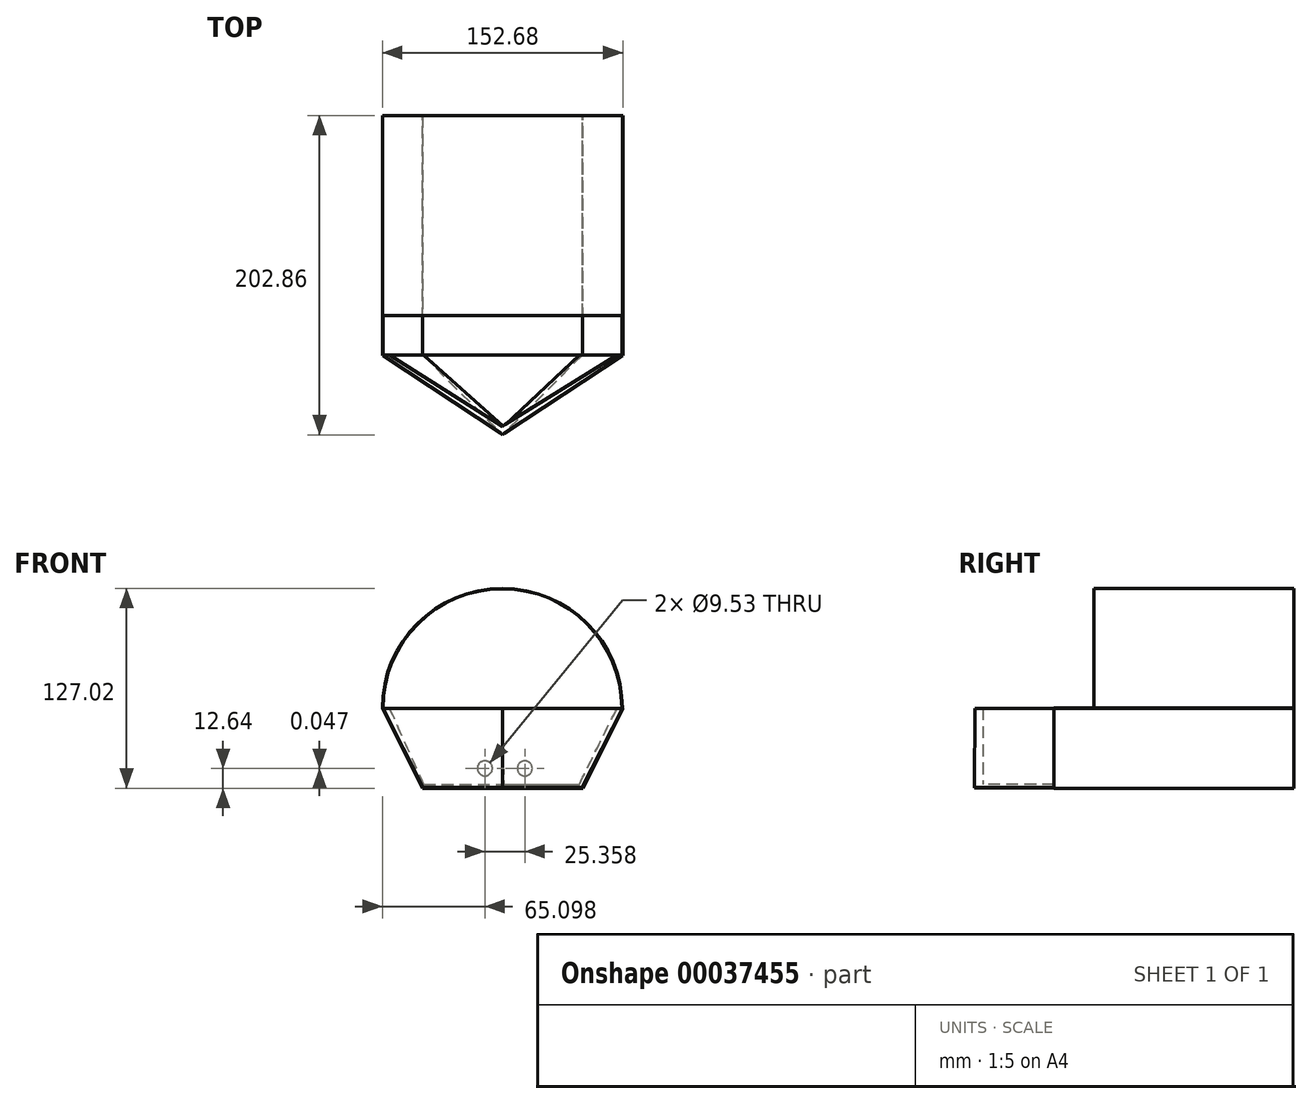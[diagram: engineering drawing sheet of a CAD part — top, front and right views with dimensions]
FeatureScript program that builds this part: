
annotation { "Feature Type Name" : "Feature", "Feature Type Description" : "" }
export const myFeature = defineFeature(function(context is Context, id is Id, definition is map)
    precondition{}
    {
        {
            var Q0;
            Q0=qCreatedBy(makeId("Top.planeOp"),FACE);
            var sketch = newSketch(context, id + "F0", { "sketchPlane" : qUnion([Q0])});
            skLineSegment(sketch, "E0.bottom", {"start": v(-53.58, 84.21) * mm, "end": v(98.82, 84.21) * mm});
            skLineSegment(sketch, "E0.top", {"start": v(-53.58, -68.19) * mm, "end": v(98.82, -68.19) * mm});
            skLineSegment(sketch, "E0.left", {"start": v(-53.58, 84.21) * mm, "end": v(-53.58, -68.19) * mm});
            skLineSegment(sketch, "E0.right", {"start": v(98.82, 84.21) * mm, "end": v(98.82, -68.19) * mm});
            skSolve(sketch);
        }
        {
            var Q0;
            Q0 = qSketchRegion(id + "F0", true);
            extrude(context, id + "F1", {"entities" : qUnion([Q0]), "depth" : 63.5 * mm});
        }
        {
            var Q0;
            Q0=makeQuery(id+"F1.opExtrude","CAP_FACE",FACE,{"disambiguationData":[OSD([sQuery(id+"F0.wireOp",EDGE,"E0.bottom"),sQuery(id+"F0.wireOp",EDGE,"E0.top"),sQuery(id+"F0.wireOp",EDGE,"E0.left"),sQuery(id+"F0.wireOp",EDGE,"E0.right")])],"isStart":false});
            var sketch = newSketch(context, id + "F2", { "sketchPlane" : qUnion([Q0])});
            skLineSegment(sketch, "E1.bottom", {"start": v(-53.26, 83.9) * mm, "end": v(98.5, 83.9) * mm});
            skLineSegment(sketch, "E1.top", {"start": v(-53.26, -67.87) * mm, "end": v(98.5, -67.87) * mm});
            skLineSegment(sketch, "E1.left", {"start": v(-53.26, 83.9) * mm, "end": v(-53.26, -67.87) * mm});
            skLineSegment(sketch, "E1.right", {"start": v(98.5, 83.9) * mm, "end": v(98.5, -67.87) * mm});
            skLineSegment(sketch, "E2", {"start": v(98.5, -5.97) * mm, "end": v(98.82, -5.97) * mm});
            skLineSegment(sketch, "E3", {"start": v(-53.26, -0.2) * mm, "end": v(-53.58, -0.2) * mm});
            skLineSegment(sketch, "E4", {"start": v(22.62, 83.9) * mm, "end": v(22.62, 84.21) * mm});
            skLineSegment(sketch, "E5", {"start": v(22.62, -67.87) * mm, "end": v(22.62, -68.19) * mm});
            skPoint(sketch, "E5.startSnap0", {"position": v(22.62, -68.19) * mm});
            skSolve(sketch);
        }
        {
            var Q0;
            Q0 = qSketchRegion(id + "F2", true);
            extrude(context, id + "F3", {"entities" : qUnion([Q0]), "operationType" : NewBodyOperationType.REMOVE, "oppositeDirection" : true, "depth" : 63.18 * mm});
        }
        {
            var Q0;
            Q0=makeQuery(id+"F1.opExtrude","CAP_FACE",FACE,{"disambiguationData":[OSD([sQuery(id+"F0.wireOp",EDGE,"E0.bottom"),sQuery(id+"F0.wireOp",EDGE,"E0.top"),sQuery(id+"F0.wireOp",EDGE,"E0.left"),sQuery(id+"F0.wireOp",EDGE,"E0.right")])],"isStart":false});
            extrude(context, id + "F4", {"entities" : qUnion([Q0]), "operationType" : NewBodyOperationType.REMOVE, "oppositeDirection" : true, "depth" : 12.7 * mm});
        }
        {
            var Q0;
            Q0=makeQuery(id+"F1.opExtrude","SWEPT_FACE",FACE,{"disambiguationData":[OSD([sQuery(id+"F0.wireOp",EDGE,"E0.bottom")])]});
            var sketch = newSketch(context, id + "F5", { "sketchPlane" : qUnion([Q0])});
            skLineSegment(sketch, "E6", {"start": v(-98.82, 50.8) * mm, "end": v(-73.42, 0) * mm});
            skLineSegment(sketch, "E7", {"start": v(53.58, 50.8) * mm, "end": v(28.18, 0) * mm});
            skLineSegment(sketch, "E8", {"start": v(28.18, 0) * mm, "end": v(-73.42, 0) * mm});
            skLineSegment(sketch, "E9", {"start": v(-73.42, 0) * mm, "end": v(-98.82, 0) * mm});
            skLineSegment(sketch, "E10", {"start": v(28.18, 0) * mm, "end": v(53.58, 0) * mm});
            skSolve(sketch);
        }
        {
            var Q0;
            Q0=makeQuery(id+"F5.imprint","IMPRINT",FACE,{"disambiguationData":[TD([[makeQuery(id+"F5.imprint","IMPRINT",EDGE,{"derivedFrom":sQuery(id+"F5.wireOp",EDGE,"E6")}),-1.0]])]});
            var Q1;
            Q1=makeQuery(id+"F5.imprint","IMPRINT",FACE,{"disambiguationData":[TD([[makeQuery(id+"F5.imprint","IMPRINT",EDGE,{"derivedFrom":sQuery(id+"F5.wireOp",EDGE,"E7")}),1.0]])]});
            extrude(context, id + "F6", {"entities" : qUnion([Q0, Q1]), "operationType" : NewBodyOperationType.REMOVE, "oppositeDirection" : true, "depth" : 609.6 * mm});
        }
        {
            var Q0;
            Q0=makeQuery(id+"F6.boolean.opBoolean","COPY",FACE,{"derivedFrom":makeQuery(id+"F6.opExtrude","SWEPT_FACE",FACE,{"disambiguationData":[OSD([sQuery(id+"F5.wireOp",EDGE,"E6")])]})});
            var sketch = newSketch(context, id + "F7", { "sketchPlane" : qUnion([Q0])});
            skLineSegment(sketch, "E11.bottom", {"start": v(-68.19, 89.63) * mm, "end": v(84.21, 89.63) * mm});
            skLineSegment(sketch, "E11.top", {"start": v(-68.19, 32.83) * mm, "end": v(84.21, 32.83) * mm});
            skLineSegment(sketch, "E11.left", {"start": v(-68.19, 89.63) * mm, "end": v(-68.19, 32.83) * mm});
            skLineSegment(sketch, "E11.right", {"start": v(84.21, 89.63) * mm, "end": v(84.21, 32.83) * mm});
            skSolve(sketch);
        }
        {
            var Q0;
            Q0 = qSketchRegion(id + "F7", true);
            extrude(context, id + "F8", {"entities" : qUnion([Q0]), "operationType" : NewBodyOperationType.ADD, "oppositeDirection" : true, "depth" : 0.16 * mm, "hasSecondDirection" : true, "secondDirectionOppositeDirection" : false, "secondDirectionDepth" : 0.16 * mm});
        }
        {
            var Q0;
            Q0=makeQuery(id+"F6.boolean.opBoolean","COPY",FACE,{"derivedFrom":makeQuery(id+"F6.opExtrude","SWEPT_FACE",FACE,{"disambiguationData":[OSD([sQuery(id+"F5.wireOp",EDGE,"E7")])]})});
            var sketch = newSketch(context, id + "F9", { "sketchPlane" : qUnion([Q0])});
            skLineSegment(sketch, "E12.bottom", {"start": v(-84.21, 69.4) * mm, "end": v(68.19, 69.4) * mm});
            skLineSegment(sketch, "E12.top", {"start": v(-84.21, 12.6) * mm, "end": v(68.19, 12.6) * mm});
            skLineSegment(sketch, "E12.left", {"start": v(-84.21, 69.4) * mm, "end": v(-84.21, 12.6) * mm});
            skLineSegment(sketch, "E12.right", {"start": v(68.19, 69.4) * mm, "end": v(68.19, 12.6) * mm});
            skSolve(sketch);
        }
        {
            var Q0;
            Q0 = qSketchRegion(id + "F9", true);
            extrude(context, id + "F10", {"entities" : qUnion([Q0]), "operationType" : NewBodyOperationType.ADD, "depth" : 0.16 * mm, "hasSecondDirection" : true, "secondDirectionOppositeDirection" : true, "secondDirectionDepth" : 0.16 * mm});
        }
        {
            var Q0;
            Q0=makeQuery(id+"F3.boolean.opBoolean","COPY",FACE,{"derivedFrom":makeQuery(id+"F3.opExtrude","CAP_FACE",FACE,{"disambiguationData":[OSD([sQuery(id+"F2.wireOp",EDGE,"E1.bottom"),sQuery(id+"F2.wireOp",EDGE,"E1.top"),sQuery(id+"F2.wireOp",EDGE,"E1.left"),sQuery(id+"F2.wireOp",EDGE,"E1.right")])],"isStart":false})});
            var sketch = newSketch(context, id + "F11", { "sketchPlane" : qUnion([Q0])});
            skLineSegment(sketch, "E13", {"start": v(-28.16, -67.87) * mm, "end": v(22.62, -118.65) * mm});
            skLineSegment(sketch, "E14", {"start": v(73.4, -67.87) * mm, "end": v(22.62, -118.65) * mm});
            skSolve(sketch);
        }
        {
            var Q0;
            Q0 = qSketchRegion(id + "F11", true);
            var Q1;
            Q1=makeQuery(id+"F11.imprint","IMPRINT",FACE,{"disambiguationData":[TD([[makeQuery(id+"F11.imprint","IMPRINT",EDGE,{"derivedFrom":sQuery(id+"F11.wireOp",EDGE,"E13")}),1.0]])]});
            extrude(context, id + "F12", {"entities" : qUnion([Q0, Q1]), "operationType" : NewBodyOperationType.ADD, "depth" : 0.32 * mm});
        }
        {
            var Q0;
            Q0=makeQuery(id+"F4.boolean.opBoolean","COPY",FACE,{"derivedFrom":makeQuery(id+"F4.opExtrude","CAP_FACE",FACE,{"disambiguationData":[OSD([sQuery(id+"F0.wireOp",EDGE,"E0.bottom"),sQuery(id+"F0.wireOp",EDGE,"E0.top"),sQuery(id+"F0.wireOp",EDGE,"E0.left"),sQuery(id+"F0.wireOp",EDGE,"E0.right")])],"isStart":false})});
            var sketch = newSketch(context, id + "F13", { "sketchPlane" : qUnion([Q0])});
            skLineSegment(sketch, "E15", {"start": v(-53.4, -68.19) * mm, "end": v(22.67, -118.4) * mm});
            skLineSegment(sketch, "E16", {"start": v(-53.4, -68.19) * mm, "end": v(98.64, -68.19) * mm});
            skLineSegment(sketch, "E17", {"start": v(98.64, -68.19) * mm, "end": v(22.67, -118.4) * mm});
            skSolve(sketch);
        }
        {
            var Q1;
            Q1=makeQuery(id+"F13.imprint","IMPRINT",FACE,{"disambiguationData":[TD([[makeQuery(id+"F13.imprint","IMPRINT",EDGE,{"derivedFrom":sQuery(id+"F13.wireOp",EDGE,"E15")}),1.0]])]});
            var Q2;
            Q2=makeQuery(id+"F12.opExtrude","CAP_FACE",FACE,{"disambiguationData":[OSD([sQuery(id+"F2.wireOp",EDGE,"E1.top"),sQuery(id+"F11.wireOp",EDGE,"E13"),sQuery(id+"F11.wireOp",EDGE,"E14")])],"isStart":false});
            loft(context, id + "F14", {"operationType" : NewBodyOperationType.ADD, "sheetProfilesArray" : [{ "sheetProfileEntities" : qUnion([Q1]) }, { "sheetProfileEntities" : qUnion([Q2]) }]});
        }
        {
            var Q0;
            Q0=makeQuery(id+"F14.boolean.opBoolean","MERGE",FACE,{"derivedFrom":[makeQuery(id+"F4.boolean.opBoolean","COPY",FACE,{"derivedFrom":makeQuery(id+"F4.opExtrude","CAP_FACE",FACE,{"disambiguationData":[OSD([sQuery(id+"F0.wireOp",EDGE,"E0.bottom"),sQuery(id+"F0.wireOp",EDGE,"E0.top"),sQuery(id+"F0.wireOp",EDGE,"E0.left"),sQuery(id+"F0.wireOp",EDGE,"E0.right")])],"isStart":false})}),makeQuery(id+"F14.opLoft","CAP_FACE",FACE,{"disambiguationData":[OSD([makeQuery(id+"F13.imprint","IMPRINT",FACE,{"disambiguationData":[TD([[makeQuery(id+"F13.imprint","IMPRINT",EDGE,{"derivedFrom":sQuery(id+"F13.wireOp",EDGE,"E15")}),1.0]])]})])],"isStart":true})]});
            var sketch = newSketch(context, id + "F15", { "sketchPlane" : qUnion([Q0])});
            skLineSegment(sketch, "E18", {"start": v(22.67, -113.2) * mm, "end": v(95.35, -67.87) * mm});
            skLineSegment(sketch, "E19", {"start": v(95.35, -67.87) * mm, "end": v(-49.32, -67.87) * mm});
            skLineSegment(sketch, "E20", {"start": v(-49.32, -67.87) * mm, "end": v(22.67, -113.2) * mm});
            skSolve(sketch);
        }
        {
            var Q0;
            Q0=makeQuery(id+"F1.opExtrude","CAP_FACE",FACE,{"disambiguationData":[OSD([sQuery(id+"F0.wireOp",EDGE,"E0.bottom"),sQuery(id+"F0.wireOp",EDGE,"E0.top"),sQuery(id+"F0.wireOp",EDGE,"E0.left"),sQuery(id+"F0.wireOp",EDGE,"E0.right")])],"isStart":true});
            cPlane(context, id + "F16", {"entities" : qUnion([Q0]), "cplaneType" : CPlaneType.OFFSET, "offset" : 2.54 * mm, "oppositeDirection" : true, "width" : 152.4 * mm, "height" : 152.4 * mm});
        }
        {
            var Q0;
            Q0=qCreatedBy(id+"F16.planeOp",FACE);
            var sketch = newSketch(context, id + "F17", { "sketchPlane" : qUnion([Q0])});
            skLineSegment(sketch, "E21", {"start": v(-28.12, 67.43) * mm, "end": v(71.86, 67.43) * mm});
            skLineSegment(sketch, "E22", {"start": v(23.14, 113.26) * mm, "end": v(71.86, 67.43) * mm});
            skLineSegment(sketch, "E23", {"start": v(-28.12, 67.43) * mm, "end": v(23.14, 113.26) * mm});
            skSolve(sketch);
        }
        {
            var Q0;
            Q0=makeQuery(id+"F10.boolean.opBoolean","MERGE",FACE,{"derivedFrom":[makeQuery(id+"F8.boolean.opBoolean","MERGE",FACE,{"derivedFrom":[makeQuery(id+"F1.opExtrude","SWEPT_FACE",FACE,{"disambiguationData":[OSD([sQuery(id+"F0.wireOp",EDGE,"E0.bottom")])]}),makeQuery(id+"F8.opExtrude","SWEPT_FACE",FACE,{"disambiguationData":[OSD([sQuery(id+"F7.wireOp",EDGE,"E11.right")])]})]}),makeQuery(id+"F10.opExtrude","SWEPT_FACE",FACE,{"disambiguationData":[OSD([sQuery(id+"F9.wireOp",EDGE,"E12.left")])]})]});
            var sketch = newSketch(context, id + "F18", { "sketchPlane" : qUnion([Q0])});
            skArc(sketch, "E24", {"start": v(53.72, 50.73) * mm, "mid": v(-22.42, 126.95) * mm, "end": v(-98.64, 50.8) * mm});
            skLineSegment(sketch, "E25", {"start": v(-98.64, 50.8) * mm, "end": v(-98.32, 50.8) * mm});
            skLineSegment(sketch, "E26", {"start": v(53.72, 50.73) * mm, "end": v(53.41, 50.8) * mm});
            skArc(sketch, "E27", {"start": v(53.41, 50.8) * mm, "mid": v(-22.45, 126.67) * mm, "end": v(-98.32, 50.8) * mm});
            skSolve(sketch);
        }
        {
            var Q0;
            Q0=makeQuery(id+"F18.imprint","IMPRINT",FACE,{"disambiguationData":[TD([[makeQuery(id+"F18.imprint","IMPRINT",EDGE,{"derivedFrom":sQuery(id+"F18.wireOp",EDGE,"E24")}),1.0]])]});
            extrude(context, id + "F19", {"entities" : qUnion([Q0]), "operationType" : NewBodyOperationType.ADD, "oppositeDirection" : true, "depth" : 127 * mm});
        }
        {
            var Q1;
            Q1=makeQuery(id+"F15.imprint","IMPRINT",FACE,{"disambiguationData":[TD([[makeQuery(id+"F15.imprint","IMPRINT",EDGE,{"derivedFrom":sQuery(id+"F15.wireOp",EDGE,"E18")}),1.0]])]});
            var Q2;
            Q2 = qSketchRegion(id + "F17", true);
            loft(context, id + "F20", {"operationType" : NewBodyOperationType.REMOVE, "sheetProfilesArray" : [{ "sheetProfileEntities" : qUnion([Q1]) }, { "sheetProfileEntities" : qUnion([Q2]) }]});
        }
        {
            var Q0;
            {var subQ0=sQuery(id+"F9.wireOp",EDGE,"E12.left");Q0=makeQuery(id+"F19.boolean.opBoolean","MERGE",FACE,{"derivedFrom":[makeQuery(id+"F10.boolean.opBoolean","MERGE",FACE,{"derivedFrom":[makeQuery(id+"F8.boolean.opBoolean","MERGE",FACE,{"derivedFrom":[makeQuery(id+"F1.opExtrude","SWEPT_FACE",FACE,{"disambiguationData":[OSD([sQuery(id+"F0.wireOp",EDGE,"E0.bottom")])]}),makeQuery(id+"F8.opExtrude","SWEPT_FACE",FACE,{"disambiguationData":[OSD([sQuery(id+"F7.wireOp",EDGE,"E11.right")])]})]}),makeQuery(id+"F10.opExtrude","SWEPT_FACE",FACE,{"disambiguationData":[OSD([subQ0])]})]}),makeQuery(id+"F19.opExtrude","CAP_FACE",FACE,{"disambiguationData":[OSD([sQuery(id+"F9.wireOp",EDGE,"E12.bottom"),subQ0,sQuery(id+"F18.wireOp",EDGE,"E24"),sQuery(id+"F18.wireOp",EDGE,"E25"),sQuery(id+"F18.wireOp",EDGE,"E27")])],"isStart":true})]});}
            var sketch = newSketch(context, id + "F21", { "sketchPlane" : qUnion([Q0])});
            skLineSegment(sketch, "E28", {"start": v(-22.42, 126.95) * mm, "end": v(-22.42, 0) * mm});
            skLineSegment(sketch, "E29", {"start": v(28.32, -0.07) * mm, "end": v(28.32, 50.8) * mm});
            skSolve(sketch);
        }
        {
            var Q0;
            Q0=makeQuery(id+"F1.opExtrude","CAP_FACE",FACE,{"disambiguationData":[OSD([sQuery(id+"F0.wireOp",EDGE,"E0.bottom"),sQuery(id+"F0.wireOp",EDGE,"E0.top"),sQuery(id+"F0.wireOp",EDGE,"E0.left"),sQuery(id+"F0.wireOp",EDGE,"E0.right")])],"isStart":true});
            var sketch = newSketch(context, id + "F22", { "sketchPlane" : qUnion([Q0])});
            skLineSegment(sketch, "E30", {"start": v(73.42, -84.21) * mm, "end": v(98.82, -84.21) * mm});
            skLineSegment(sketch, "E31", {"start": v(-28.18, -84.21) * mm, "end": v(-53.58, -84.21) * mm});
            skLineSegment(sketch, "E32", {"start": v(-28.18, -84.21) * mm, "end": v(73.42, -84.21) * mm});
            skSolve(sketch);
        }
        {
            var Q0;
            {var subQ9=sQuery(id+"F7.wireOp",EDGE,"E11.right");Q0=makeQuery(id+"F21.imprint","IMPRINT",FACE,{"disambiguationData":[TD([[makeQuery(id+"F21.imprint","IMPRINT",EDGE,{"derivedFrom":makeQuery(id+"F8.opExtrude","CAP_EDGE",EDGE,{"disambiguationData":[OSD([subQ9])],"isStart":true})}),1.0]])]});}
            var sketch = newSketch(context, id + "F23", { "sketchPlane" : qUnion([Q0])});
            skCircle(sketch, "E33", {"center": v(-36.74, 12.57) * mm, "radius": 4.76 * mm});
            skSolve(sketch);
        }
        {
            var Q0;
            Q0=sQuery(id+"F23.wireOp",VERTEX,"E33.center");
            var Q1;
            Q1=makeQuery(id+"F1.opExtrude","SWEPT_BODY",BODY,{"disambiguationData":[OSD([sQuery(id+"F0.wireOp",EDGE,"E0.bottom"),sQuery(id+"F0.wireOp",EDGE,"E0.top"),sQuery(id+"F0.wireOp",EDGE,"E0.left"),sQuery(id+"F0.wireOp",EDGE,"E0.right")])]});
            hole(context, id + "F24", {"style" : HoleStyle.SIMPLE, "holeDiameter" : 9.52 * mm, "endStyle" : HoleEndStyle.BLIND, "holeDepth" : 38.1 * mm, "locations" : qUnion([Q0]), "scope" : qUnion([Q1])});
        }
        {
            var Q0;
            {var subQ4=sQuery(id+"F21.wireOp",EDGE,"E29");Q0=makeQuery(id+"F21.imprint","IMPRINT",FACE,{"disambiguationData":[TD([[makeQuery(id+"F21.imprint","IMPRINT",EDGE,{"derivedFrom":subQ4}),1.0]])]});}
            var sketch = newSketch(context, id + "F25", { "sketchPlane" : qUnion([Q0])});
            skCircle(sketch, "E34", {"center": v(-11.38, 12.62) * mm, "radius": 4.76 * mm});
            skLineSegment(sketch, "E35", {"start": v(-36.78, 12.62) * mm, "end": v(-11.38, 12.62) * mm});
            skSolve(sketch);
        }
        {
            var Q0;
            Q0=makeQuery(id+"F25.imprint","IMPRINT",FACE,{"disambiguationData":[TD([[makeQuery(id+"F25.imprint","IMPRINT",EDGE,{"derivedFrom":sQuery(id+"F25.wireOp",EDGE,"E34")}),1.0]])]});
            extrude(context, id + "F26", {"entities" : qUnion([Q0]), "operationType" : NewBodyOperationType.REMOVE, "oppositeDirection" : true, "depth" : 25.4 * mm});
        }
    });
